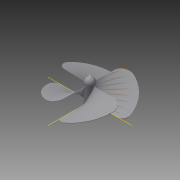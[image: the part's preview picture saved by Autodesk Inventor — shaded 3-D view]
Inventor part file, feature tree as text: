
AUTODESK INVENTOR PART (.ipt)
format: ipt  version: 2015 (Build 190159000, 159)  size: 628,224 bytes
history: native  units: mm
features: fillet x4, sketch x3, other x2, extrude x1, thicken_offset x1, pattern_circular x1, sweep x1
ambient origin geometry x8: Origin, YZ Plane, XZ Plane, XY Plane, X Axis, Y Axis, Z Axis, Center Point
bodies: Solid1 (feature_tree)
feature tree (13):
  extrude  "Extrusion1"  Depth=70.0mm TaperAngle=0.0deg
  fillet  "Fillet1"  Radius=15.0mm
  thicken_offset  "Thicken1"
  fillet  "Fillet2"  Radius=14.0mm
  fillet  "Fillet3"  Radius=101.0mm
  fillet  "Fillet4"  [1 undecoded]
  pattern_circular  "Circular Pattern1"  [2 undecoded]
  sketch  "Sketch1"  dims[d0=30.0mm d1=70.0mm d2=5.0mm d3=0.0mm d4=0.0mm d5=15.0mm d6=14.0mm d7=101.0mm]
  sketch  "Sketch2"  dims[d16=50.0mm d17=2.5mm d18=30.0mm d19=0.0mm d20=0.0mm d21=0.0mm d22=1.0mm d23=1.0mm d24=20.0mm d25=30.0mm d26=3.0mm d27=40.0mm d28=360.0deg]
  sketch  "3D Sketch6"
  other  "Helical Curve3"
  other  "Srf1"
  sweep  "SweepSrf1"
note: 3 required parameter values undecoded (feature->parameter linkage not recoverable at this tier; creation-order binding heuristic only, values carry confidence <= 0.55)
